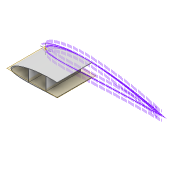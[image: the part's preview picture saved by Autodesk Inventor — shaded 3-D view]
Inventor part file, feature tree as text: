
AUTODESK INVENTOR PART (.ipt)
format: ipt  version: 2022 (Build 260153000, 153)  size: 341,504 bytes
history: native  units: mm
features: extrude x3, sketch x3, shell x1
ambient origin geometry x8: Origin, YZ Plane, XZ Plane, XY Plane, X Axis, Y Axis, Z Axis, Center Point
bodies: Solid1 (feature_tree)
feature tree (7):
  extrude  "Extrusion1"  Depth=2.0mm
  shell  "Shell1"  Thickness=2.0mm
  extrude  "Extrusion15"  Depth=150.0mm TaperAngle=0.0deg
  extrude  "Extrusion16"  Depth=300.0mm TaperAngle=0.0deg
  sketch  "Sketch3"  dims[d0=150.0mm d1=0.0mm d2=2.0mm d115=2.0mm]
  sketch  "Sketch33"  dims[d116=150.0mm d117=150.0mm d118=0.0mm]
  sketch  "Sketch34"  dims[d119=200.0mm d120=300.0mm d121=0.0mm d122=2.0mm]
